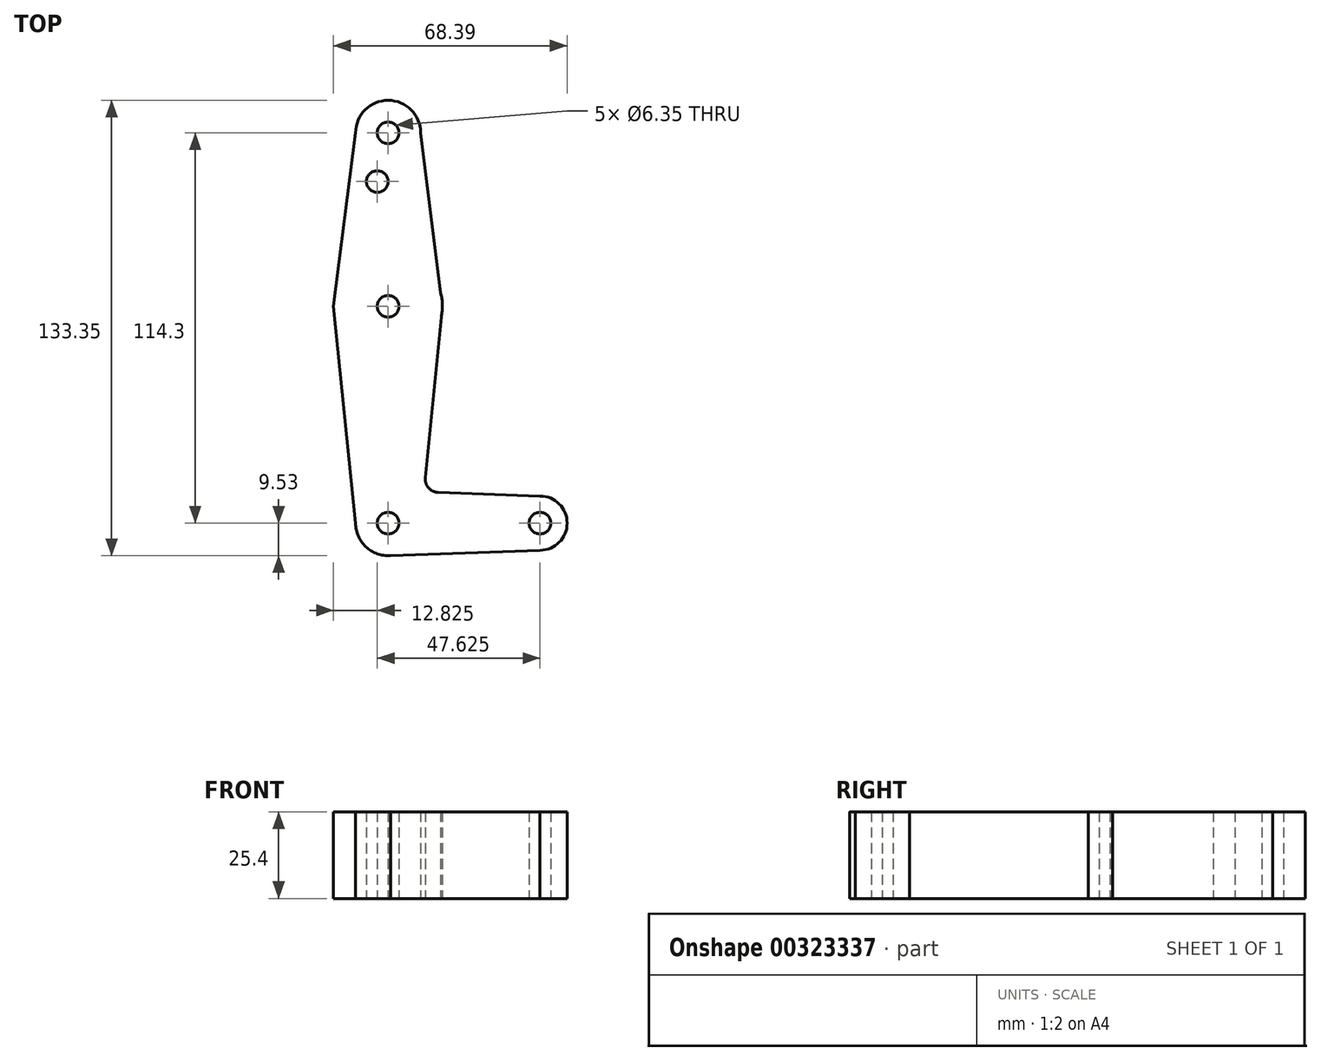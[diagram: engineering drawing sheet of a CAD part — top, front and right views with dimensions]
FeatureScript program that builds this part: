
annotation { "Feature Type Name" : "Feature", "Feature Type Description" : "" }
export const myFeature = defineFeature(function(context is Context, id is Id, definition is map)
    precondition{}
    {
        {
            var Q0;
            Q0=qCreatedBy(makeId("Top.planeOp"),FACE);
            var sketch = newSketch(context, id + "F0", { "sketchPlane" : qUnion([Q0])});
            skLineSegment(sketch, "E0", {"start": v(0, 50.8) * mm, "end": v(0, 0) * mm});
            skLineSegment(sketch, "E1", {"start": v(0, 0) * mm, "end": v(0, -63.5) * mm});
            skLineSegment(sketch, "E2", {"start": v(0, -63.5) * mm, "end": v(44.45, -63.5) * mm});
            skCircle(sketch, "E3", {"center": v(0, 50.8) * mm, "radius": 9.53 * mm});
            skCircle(sketch, "E4", {"center": v(0, 0) * mm, "radius": 15.88 * mm});
            skArc(sketch, "E5", {"start": v(0, -53.98) * mm, "mid": v(-0.34, -73.02) * mm, "end": v(0.68, -54) * mm});
            skCircle(sketch, "E6", {"center": v(44.45, -63.5) * mm, "radius": 7.94 * mm});
            skLineSegment(sketch, "E7", {"start": v(-9.53, 50.8) * mm, "end": v(-16, 0) * mm});
            skLineSegment(sketch, "E8", {"start": v(-16, 0) * mm, "end": v(-9.53, -63.5) * mm});
            skLineSegment(sketch, "E9", {"start": v(9.52, 50.8) * mm, "end": v(15.88, 0) * mm});
            skLineSegment(sketch, "E10", {"start": v(15.88, 0) * mm, "end": v(10.86, -50.13) * mm});
            skLineSegment(sketch, "E11", {"start": v(0, -73.02) * mm, "end": v(44.45, -71.44) * mm});
            skLineSegment(sketch, "E12", {"start": v(44.45, -71.44) * mm, "end": v(44.45, -55.56) * mm});
            skLineSegment(sketch, "E13", {"start": v(44.45, -55.56) * mm, "end": v(14.68, -54.5) * mm});
            skCircle(sketch, "E14", {"center": v(0, 50.8) * mm, "radius": 3.18 * mm});
            skCircle(sketch, "E15", {"center": v(0, 0) * mm, "radius": 3.18 * mm});
            skCircle(sketch, "E16", {"center": v(0, -63.5) * mm, "radius": 3.18 * mm});
            skCircle(sketch, "E17", {"center": v(44.45, -63.5) * mm, "radius": 3.18 * mm});
            skArc(sketch, "E18", {"start": v(10.86, -50.13) * mm, "mid": v(11.82, -53.14) * mm, "end": v(14.68, -54.5) * mm});
            skLineSegment(sketch, "E19.trimOffspring", {"start": v(0.68, -54) * mm, "end": v(0, -53.98) * mm});
            skCircle(sketch, "E20", {"center": v(-3.17, 36.53) * mm, "radius": 3.18 * mm});
            skSolve(sketch);
        }
        {
            var Q0;
            Q0 = qSketchRegion(id + "F0", true);
            var Q1;
            {var subQ7=sQuery(id+"F0.wireOp",EDGE,"E19.trimOffspring");Q1=makeQuery(id+"F0.imprint","IMPRINT",FACE,{"disambiguationData":[TD([[makeQuery(id+"F0.imprint","IMPRINT",EDGE,{"derivedFrom":subQ7}),1.0]])]});}
            extrude(context, id + "F1", {"entities" : qUnion([Q0, Q1]), "depth" : 25.4 * mm});
        }
    });
